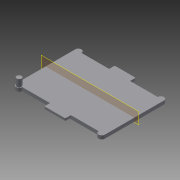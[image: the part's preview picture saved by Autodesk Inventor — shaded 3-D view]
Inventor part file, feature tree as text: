
AUTODESK INVENTOR PART (.ipt)
format: ipt  version: 2013 (Build 170138000, 138)  size: 119,808 bytes
history: native  units: mm
features: extrude x3, sketch x3, plane x1, mirror x1, fillet x1
ambient origin geometry x8: Origin, YZ Plane, XZ Plane, XY Plane, X Axis, Y Axis, Z Axis, Center Point
feature tree (9):
  extrude  "Extrusion2"  Depth=84.8mm
  extrude  "Extrusion3"  Depth=5.0mm TaperAngle=0.0deg
  extrude  "Extrusion4"  Depth=10.0mm TaperAngle=0.0deg
  plane  "Work Plane1"
  mirror  "Mirror1"
  fillet  "Fillet1"  Radius=1.8mm
  sketch  "Sketch1"  dims[d2=127.1mm d4=84.8mm]
  sketch  "Sketch2"  dims[d10=4.4mm d12=5.0mm d13=0.0mm]
  sketch  "Sketch3"  dims[d14=7.0mm d16=10.0mm d17=0.0mm d18=1.8mm d19=15.0mm d20=8.0mm d21=0.0mm d22=1.0mm]
